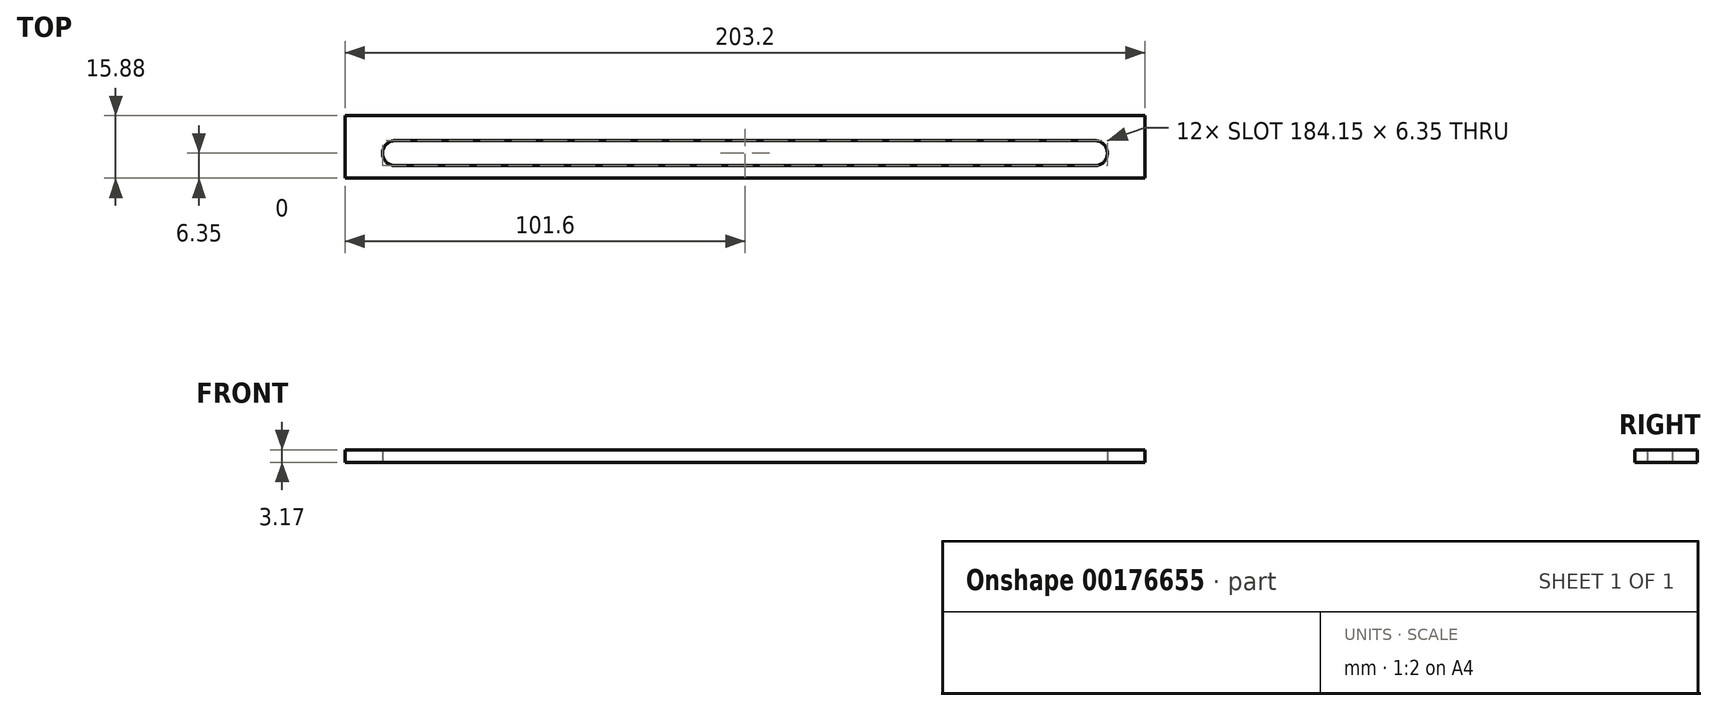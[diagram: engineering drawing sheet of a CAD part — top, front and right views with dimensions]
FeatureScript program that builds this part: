
annotation { "Feature Type Name" : "Feature", "Feature Type Description" : "" }
export const myFeature = defineFeature(function(context is Context, id is Id, definition is map)
    precondition{}
    {
        {
            var Q0;
            Q0=qCreatedBy(makeId("Top.planeOp"),FACE);
            var sketch = newSketch(context, id + "F0", { "sketchPlane" : qUnion([Q0])});
            skLineSegment(sketch, "E0.bottom", {"start": v(0, 0) * mm, "end": v(-203.2, 0) * mm});
            skLineSegment(sketch, "E0.top", {"start": v(0, 15.88) * mm, "end": v(-203.2, 15.88) * mm});
            skLineSegment(sketch, "E0.left", {"start": v(0, 0) * mm, "end": v(0, 15.88) * mm});
            skLineSegment(sketch, "E0.right", {"start": v(-203.2, 0) * mm, "end": v(-203.2, 15.88) * mm});
            skLineSegment(sketch, "E1.bottom", {"start": v(-190.5, 9.52) * mm, "end": v(-12.7, 9.53) * mm});
            skLineSegment(sketch, "E1.top", {"start": v(-190.5, 3.17) * mm, "end": v(-12.7, 3.18) * mm});
            skArc(sketch, "E2", {"start": v(-190.5, 9.52) * mm, "mid": v(-193.68, 6.35) * mm, "end": v(-190.5, 3.17) * mm});
            skArc(sketch, "E3", {"start": v(-12.7, 3.18) * mm, "mid": v(-9.53, 6.35) * mm, "end": v(-12.7, 9.53) * mm});
            skSolve(sketch);
        }
        {
            var Q0;
            Q0 = qSketchRegion(id + "F0", true);
            extrude(context, id + "F1", {"entities" : qUnion([Q0]), "depth" : 3.17 * mm});
        }
    });
